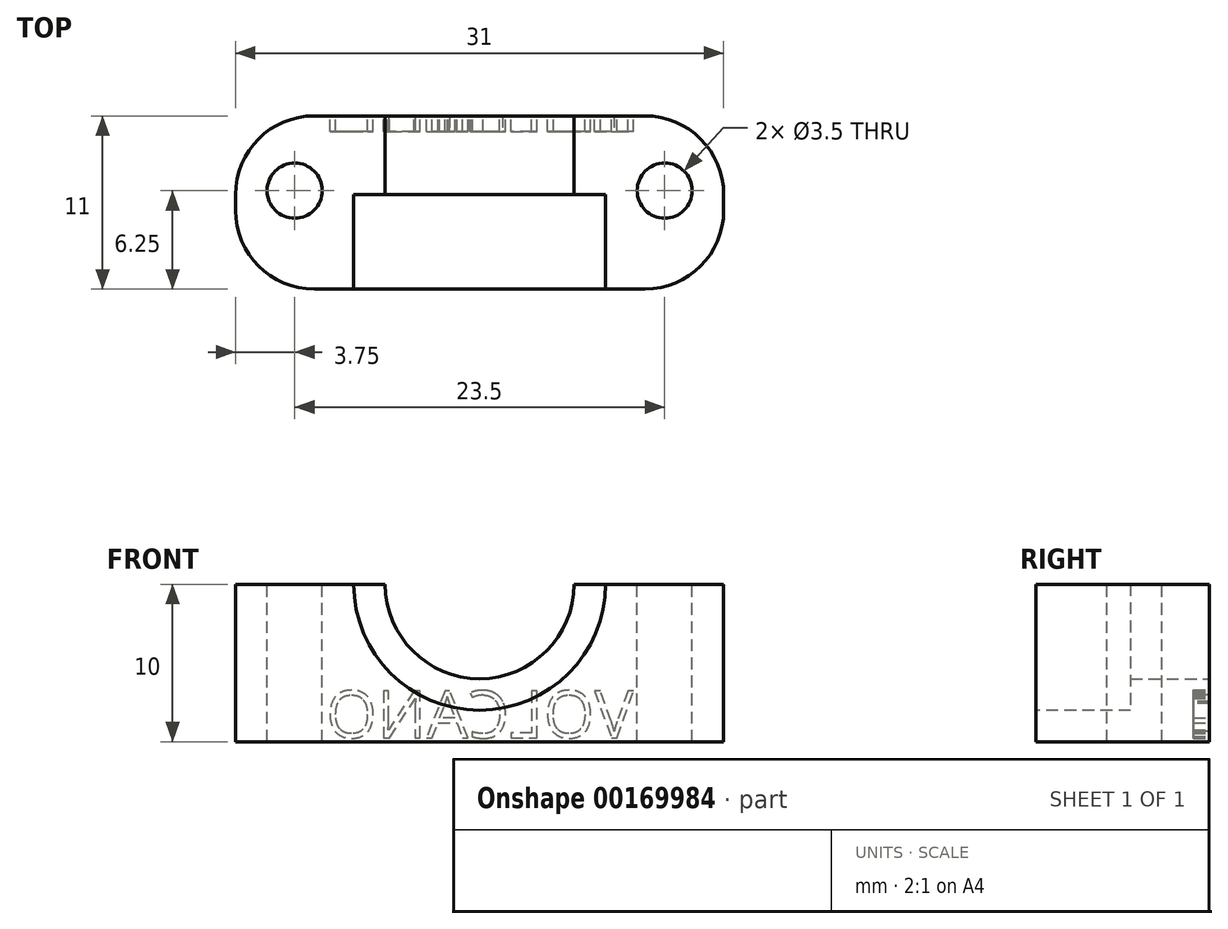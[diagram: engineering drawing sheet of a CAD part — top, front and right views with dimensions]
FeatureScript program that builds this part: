
annotation { "Feature Type Name" : "Feature", "Feature Type Description" : "" }
export const myFeature = defineFeature(function(context is Context, id is Id, definition is map)
    precondition{}
    {
        {
            var Q0;
            Q0=qCreatedBy(makeId("Top.planeOp"),FACE);
            var sketch = newSketch(context, id + "F0", { "sketchPlane" : qUnion([Q0])});
            skLineSegment(sketch, "E0.bottom", {"start": v(0, 0) * mm, "end": v(25, 0) * mm});
            skLineSegment(sketch, "E0.top", {"start": v(0, 11) * mm, "end": v(25, 11) * mm});
            skLineSegment(sketch, "E0.left", {"start": v(0, 0) * mm, "end": v(0, 11) * mm});
            skLineSegment(sketch, "E0.right", {"start": v(25, 0) * mm, "end": v(25, 11) * mm});
            skSolve(sketch);
        }
        {
            var Q0;
            Q0=qSketchRegion(id+"F0",true);
            extrude(context, id + "F1", {"entities" : qUnion([Q0]), "depth" : 10 * mm});
        }
        {
            var Q0;
            Q0=makeQuery(id+"F1.opExtrude","SWEPT_FACE",FACE,{"disambiguationData":[OSD([sQuery(id+"F0.wireOp",EDGE,"E0.bottom")])]});
            var sketch = newSketch(context, id + "F2", { "sketchPlane" : qUnion([Q0])});
            skCircle(sketch, "E1", {"center": v(12.5, 10) * mm, "radius": 8 * mm});
            skSolve(sketch);
        }
        {
            var Q0;
            Q0=qSketchRegion(id+"F2",true);
            extrude(context, id + "F3", {"entities" : qUnion([Q0]), "operationType" : NewBodyOperationType.REMOVE, "oppositeDirection" : true, "depth" : 6 * mm});
        }
        {
            var Q0;
            Q0=makeQuery(id+"F1.opExtrude","SWEPT_FACE",FACE,{"disambiguationData":[OSD([sQuery(id+"F0.wireOp",EDGE,"E0.top")])]});
            var sketch = newSketch(context, id + "F4", { "sketchPlane" : qUnion([Q0])});
            skCircle(sketch, "E2", {"center": v(-12.5, 10) * mm, "radius": 6 * mm});
            skSolve(sketch);
        }
        {
            var Q0;
            Q0=qSketchRegion(id+"F4",true);
            extrude(context, id + "F5", {"entities" : qUnion([Q0]), "operationType" : NewBodyOperationType.REMOVE, "oppositeDirection" : true, "depth" : 6 * mm});
        }
        {
            var Q0;
            Q0=makeQuery(id+"F1.opExtrude","SWEPT_FACE",FACE,{"disambiguationData":[OSD([sQuery(id+"F0.wireOp",EDGE,"E0.left")])]});
            var sketch = newSketch(context, id + "F6", { "sketchPlane" : qUnion([Q0])});
            skLineSegment(sketch, "E3.bottom", {"start": v(-11, 0) * mm, "end": v(0, 0) * mm});
            skLineSegment(sketch, "E3.top", {"start": v(-11, 10) * mm, "end": v(0, 10) * mm});
            skLineSegment(sketch, "E3.left", {"start": v(-11, 0) * mm, "end": v(-11, 10) * mm});
            skLineSegment(sketch, "E3.right", {"start": v(0, 0) * mm, "end": v(0, 10) * mm});
            skSolve(sketch);
        }
        {
            var Q0;
            Q0=qSketchRegion(id+"F6",true);
            extrude(context, id + "F7", {"entities" : qUnion([Q0]), "operationType" : NewBodyOperationType.ADD, "depth" : 3 * mm});
        }
        {
            var Q0;
            Q0=makeQuery(id+"F1.opExtrude","SWEPT_FACE",FACE,{"disambiguationData":[OSD([sQuery(id+"F0.wireOp",EDGE,"E0.right")])]});
            var sketch = newSketch(context, id + "F8", { "sketchPlane" : qUnion([Q0])});
            skLineSegment(sketch, "E4.bottom", {"start": v(11, 10) * mm, "end": v(0, 10) * mm});
            skLineSegment(sketch, "E4.top", {"start": v(11, 0) * mm, "end": v(0, 0) * mm});
            skLineSegment(sketch, "E4.left", {"start": v(11, 10) * mm, "end": v(11, 0) * mm});
            skLineSegment(sketch, "E4.right", {"start": v(0, 10) * mm, "end": v(0, 0) * mm});
            skSolve(sketch);
        }
        {
            var Q0;
            Q0=qSketchRegion(id+"F8",true);
            extrude(context, id + "F9", {"entities" : qUnion([Q0]), "operationType" : NewBodyOperationType.ADD, "depth" : 3 * mm});
        }
        {
            var Q0;
            Q0=makeQuery(id+"F9.opExtrude","CAP_EDGE",EDGE,{"disambiguationData":[OSD([sQuery(id+"F8.wireOp",EDGE,"E4.left")])],"isStart":false});
            var Q1;
            Q1=makeQuery(id+"F9.opExtrude","CAP_EDGE",EDGE,{"disambiguationData":[OSD([sQuery(id+"F8.wireOp",EDGE,"E4.right")])],"isStart":false});
            var Q2;
            Q2=makeQuery(id+"F7.opExtrude","CAP_EDGE",EDGE,{"disambiguationData":[OSD([sQuery(id+"F6.wireOp",EDGE,"E3.left")])],"isStart":false});
            var Q3;
            Q3=makeQuery(id+"F7.opExtrude","CAP_EDGE",EDGE,{"disambiguationData":[OSD([sQuery(id+"F6.wireOp",EDGE,"E3.right")])],"isStart":false});
            fillet(context, id + "F10", {"entities" : qUnion([Q0, Q1, Q2, Q3]), "radius" : 5 * mm, "tangentPropagation" : true, "allowEdgeOverflow" : false});
        }
        {
            var Q0;
            {var subQ0=sQuery(id+"F0.wireOp",EDGE,"E0.bottom");var subQ1=sQuery(id+"F0.wireOp",EDGE,"E0.top");var subQ2=sQuery(id+"F0.wireOp",EDGE,"E0.left");Q0=makeQuery(id+"F5.boolean.opBoolean","SPLIT",FACE,{"disambiguationData":[TD([makeQuery(id+"F1.opExtrude","SWEPT_FACE",FACE,{"disambiguationData":[OSD([subQ2])]})])],"derivedFrom":makeQuery(id+"F1.opExtrude","CAP_FACE",FACE,{"disambiguationData":[OSD([subQ0,subQ1,subQ2,sQuery(id+"F0.wireOp",EDGE,"E0.right")])],"isStart":false})});}
            var sketch = newSketch(context, id + "F11", { "sketchPlane" : qUnion([Q0])});
            skCircle(sketch, "E5", {"center": v(0.75, 6.25) * mm, "radius": 1.75 * mm});
            skCircle(sketch, "E6", {"center": v(24.25, 6.25) * mm, "radius": 1.75 * mm});
            skSolve(sketch);
        }
        {
            var Q0;
            Q0=qSketchRegion(id+"F11",true);
            extrude(context, id + "F12", {"entities" : qUnion([Q0]), "operationType" : NewBodyOperationType.REMOVE, "oppositeDirection" : true, "depth" : 25 * mm});
        }
        {
            var Q0;
            Q0=makeQuery(id+"F9.boolean.opBoolean","MERGE",FACE,{"derivedFrom":[makeQuery(id+"F7.boolean.opBoolean","MERGE",FACE,{"derivedFrom":[makeQuery(id+"F1.opExtrude","SWEPT_FACE",FACE,{"disambiguationData":[OSD([sQuery(id+"F0.wireOp",EDGE,"E0.top")])]}),makeQuery(id+"F7.opExtrude","SWEPT_FACE",FACE,{"disambiguationData":[OSD([sQuery(id+"F6.wireOp",EDGE,"E3.left")])]})]}),makeQuery(id+"F9.opExtrude","SWEPT_FACE",FACE,{"disambiguationData":[OSD([sQuery(id+"F8.wireOp",EDGE,"E4.left")])]})]});
            var sketch = newSketch(context, id + "F13", { "sketchPlane" : qUnion([Q0])});
            skText(sketch, "E7", { "text": "VOLCANO", "fontName": "OpenSans-Regular.ttf"});
            const initialGuessF13  = {"E7": [-0.02228, 0.00025, 1, 0, 0.003]};
            skSetInitialGuess(sketch, initialGuessF13);
            skSolve(sketch);
        }
        {
            var Q0;
            Q0 = qSketchRegion(id + "F13", true);
            extrude(context, id + "F14", {"entities" : qUnion([Q0]), "operationType" : NewBodyOperationType.REMOVE, "oppositeDirection" : true, "depth" : 1 * mm});
        }
    });
